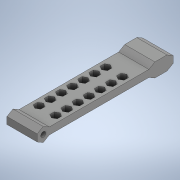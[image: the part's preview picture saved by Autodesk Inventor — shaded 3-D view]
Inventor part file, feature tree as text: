
AUTODESK INVENTOR PART (.ipt)
format: ipt  version: 2020 (Build 240168000, 168)  size: 326,656 bytes
history: native  units: in
note: dims shown in document units (in); Inventor stores cm internally (conversion verified against a paired STEP export)
features: sketch x4, extrude x3, plane x1, projected_geometry x1
ambient origin geometry x8: Origin, YZ Plane, XZ Plane, XY Plane, X Axis, Y Axis, Z Axis, Center Point
bodies: Solid1 (feature_tree)
feature tree (9):
  extrude  "Extrusion1"  Depth=3.5433in
  plane  "Work Plane1"
  extrude  "Extrusion2"  Depth=0.7874in
  extrude  "Extrusion3"  Depth=0.0787in
  sketch  "Sketch4"  dims[d6=0.7874in d7=0.0in d8=0.0787in d9=0.0787in d10=0.0787in d11=0.2273in d12=3.937in d14=0.2903in d15=0.3937in d17=0.3937in d19=3.937in d21=0.2903in d22=0.3937in d24=0.3937in d26=0.7874in d27=0.0in d28=3.2283in d29=0.315in d30=0.315in d31=0.315in]
  sketch  "Sketch1"  dims[d0=0.1818in d1=3.5433in]
  sketch  "Sketch2"  dims[d2=0.1299in d3=0.7874in]
  sketch  "Sketch3"  dims[d4=0.0in d5=0.0787in]
  projected_geometry  "Projected Loop1"
